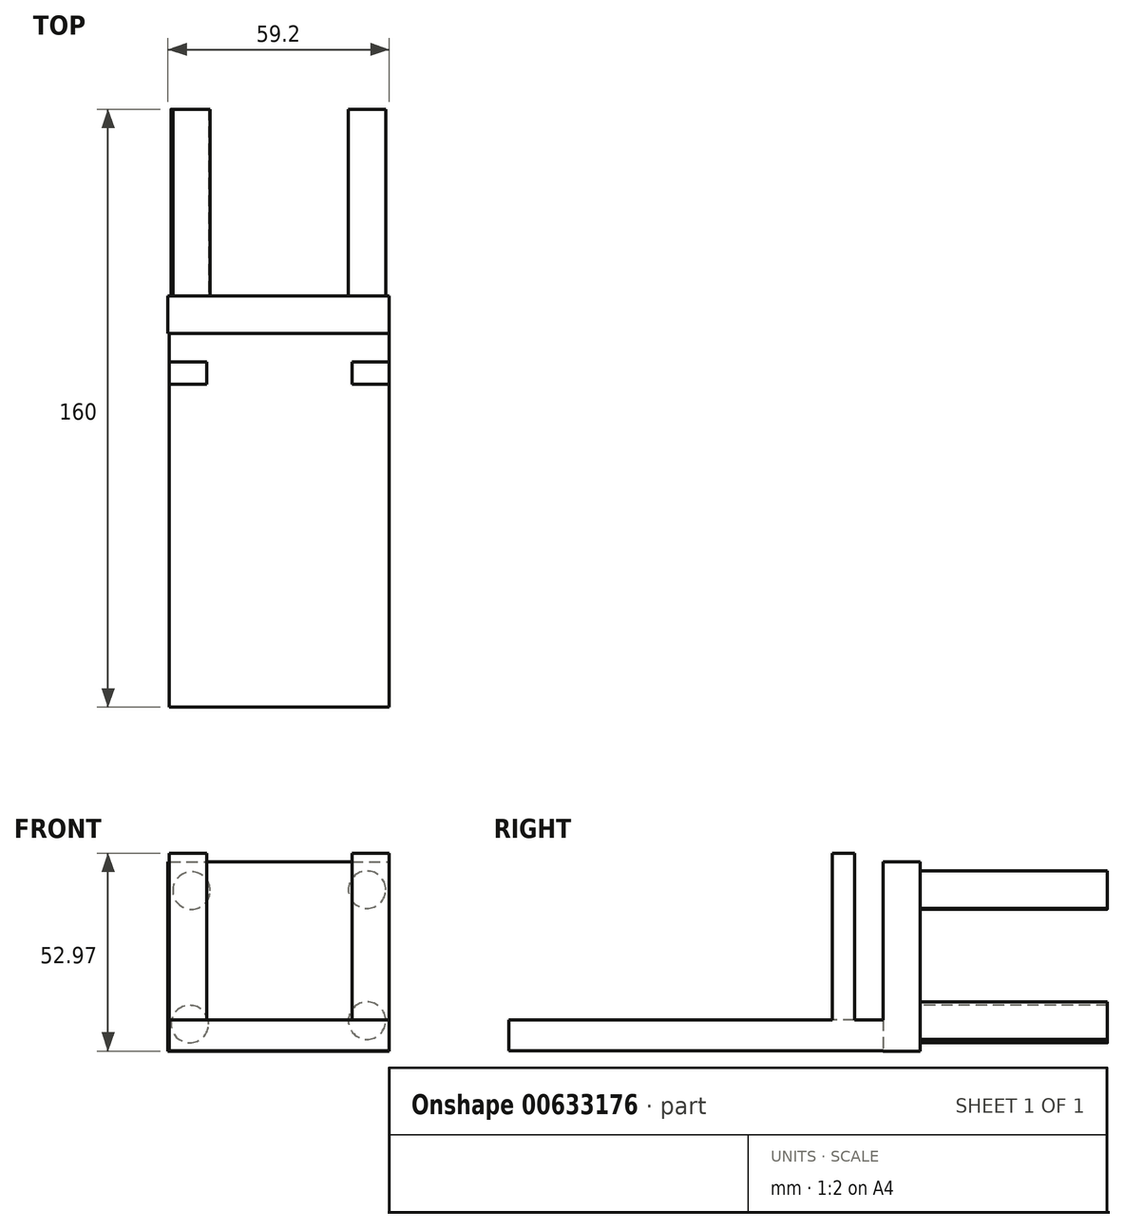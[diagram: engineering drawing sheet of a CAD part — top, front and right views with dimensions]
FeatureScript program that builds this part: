
annotation { "Feature Type Name" : "Feature", "Feature Type Description" : "" }
export const myFeature = defineFeature(function(context is Context, id is Id, definition is map)
    precondition{}
    {
        {
            var Q0;
            Q0=qCreatedBy(makeId("Front.planeOp"),FACE);
            var sketch = newSketch(context, id + "F0", { "sketchPlane" : qUnion([Q0])});
            skLineSegment(sketch, "E0.bottom", {"start": v(-35.04, 17.85) * mm, "end": v(24.16, 17.85) * mm});
            skLineSegment(sketch, "E0.top", {"start": v(-35.04, -32.75) * mm, "end": v(24.16, -32.75) * mm});
            skLineSegment(sketch, "E0.left", {"start": v(-35.04, 17.85) * mm, "end": v(-35.04, -32.75) * mm});
            skLineSegment(sketch, "E0.right", {"start": v(24.16, 17.85) * mm, "end": v(24.16, -32.75) * mm});
            skSolve(sketch);
        }
        {
            var Q0;
            Q0 = qSketchRegion(id + "F0", true);
            extrude(context, id + "F1", {"entities" : qUnion([Q0]), "depth" : 10 * mm, "offsetDistance" : 25.4 * mm});
        }
        {
            var Q0;
            Q0=makeQuery(id+"F1.opExtrude","CAP_FACE",FACE,{"disambiguationData":[OSD([sQuery(id+"F0.wireOp",EDGE,"E0.bottom"),sQuery(id+"F0.wireOp",EDGE,"E0.top"),sQuery(id+"F0.wireOp",EDGE,"E0.left"),sQuery(id+"F0.wireOp",EDGE,"E0.right")])],"isStart":false});
            var sketch = newSketch(context, id + "F2", { "sketchPlane" : qUnion([Q0])});
            skLineSegment(sketch, "E1.bottom", {"start": v(-30.92, 12.5) * mm, "end": v(20.4, 12.5) * mm});
            skLineSegment(sketch, "E1.top", {"start": v(-30.92, -27.72) * mm, "end": v(20.4, -27.72) * mm});
            skLineSegment(sketch, "E1.left", {"start": v(-30.92, 12.5) * mm, "end": v(-30.92, -27.72) * mm});
            skLineSegment(sketch, "E1.right", {"start": v(20.4, 12.5) * mm, "end": v(20.4, -27.72) * mm});
            skSolve(sketch);
        }
        {
            var Q0;
            Q0=makeQuery(id+"F1.opExtrude","CAP_FACE",FACE,{"disambiguationData":[OSD([sQuery(id+"F0.wireOp",EDGE,"E0.bottom"),sQuery(id+"F0.wireOp",EDGE,"E0.top"),sQuery(id+"F0.wireOp",EDGE,"E0.left"),sQuery(id+"F0.wireOp",EDGE,"E0.right")])],"isStart":true});
            var sketch = newSketch(context, id + "F3", { "sketchPlane" : qUnion([Q0])});
            skCircle(sketch, "E2", {"center": v(-18.2, 10.42) * mm, "radius": 5 * mm});
            skCircle(sketch, "E3", {"center": v(28.73, 10.19) * mm, "radius": 5 * mm});
            skCircle(sketch, "E4", {"center": v(-18.2, -24.6) * mm, "radius": 5 * mm});
            skCircle(sketch, "E5", {"center": v(29.19, -25.53) * mm, "radius": 5 * mm});
            skSolve(sketch);
        }
        {
            var Q0;
            Q0 = qSketchRegion(id + "F3", true);
            extrude(context, id + "F4", {"entities" : qUnion([Q0]), "depth" : 50 * mm, "offsetDistance" : 25 * mm});
        }
        {
            var Q0;
            Q0=makeQuery(id+"F2.imprint","IMPRINT",FACE,{"disambiguationData":[TD([[makeQuery(id+"F2.imprint","IMPRINT",EDGE,{"derivedFrom":sQuery(id+"F2.wireOp",EDGE,"E1.bottom")}),1.0]])]});
            var sketch = newSketch(context, id + "F5", { "sketchPlane" : qUnion([Q0])});
            skLineSegment(sketch, "E6.bottom", {"start": v(-34.68, -24.38) * mm, "end": v(24.15, -24.38) * mm});
            skLineSegment(sketch, "E6.top", {"start": v(-34.68, -32.62) * mm, "end": v(24.15, -32.62) * mm});
            skLineSegment(sketch, "E6.left", {"start": v(-34.68, -24.38) * mm, "end": v(-34.68, -32.62) * mm});
            skLineSegment(sketch, "E6.right", {"start": v(24.15, -24.38) * mm, "end": v(24.15, -32.62) * mm});
            skSolve(sketch);
        }
        {
            var Q0;
            Q0 = qSketchRegion(id + "F5", true);
            extrude(context, id + "F6", {"entities" : qUnion([Q0]), "operationType" : NewBodyOperationType.ADD, "depth" : 100 * mm, "offsetDistance" : 25 * mm});
        }
        {
            var Q0;
            Q0=makeQuery(id+"F6.opExtrude","SWEPT_FACE",FACE,{"disambiguationData":[OSD([sQuery(id+"F5.wireOp",EDGE,"E6.bottom")])]});
            var sketch = newSketch(context, id + "F7", { "sketchPlane" : qUnion([Q0])});
            skLineSegment(sketch, "E7.bottom", {"start": v(-34.68, -17.64) * mm, "end": v(-24.68, -17.64) * mm});
            skLineSegment(sketch, "E7.top", {"start": v(-34.68, -23.57) * mm, "end": v(-24.68, -23.57) * mm});
            skLineSegment(sketch, "E7.left", {"start": v(-34.68, -17.64) * mm, "end": v(-34.68, -23.57) * mm});
            skLineSegment(sketch, "E7.right", {"start": v(-24.68, -17.64) * mm, "end": v(-24.68, -23.57) * mm});
            skLineSegment(sketch, "E8", {"start": v(-34.68, -17.64) * mm, "end": v(24.15, -17.64) * mm});
            skLineSegment(sketch, "E9.bottom", {"start": v(14.15, -17.64) * mm, "end": v(24.15, -17.64) * mm});
            skLineSegment(sketch, "E9.top", {"start": v(14.15, -23.57) * mm, "end": v(24.15, -23.57) * mm});
            skLineSegment(sketch, "E9.left", {"start": v(14.15, -17.64) * mm, "end": v(14.15, -23.57) * mm});
            skLineSegment(sketch, "E9.right", {"start": v(24.15, -17.64) * mm, "end": v(24.15, -23.57) * mm});
            skSolve(sketch);
        }
        {
            var Q0;
            Q0 = qSketchRegion(id + "F7", true);
            extrude(context, id + "F8", {"entities" : qUnion([Q0]), "operationType" : NewBodyOperationType.ADD, "depth" : 44.6 * mm, "offsetDistance" : 25 * mm});
        }
    });
